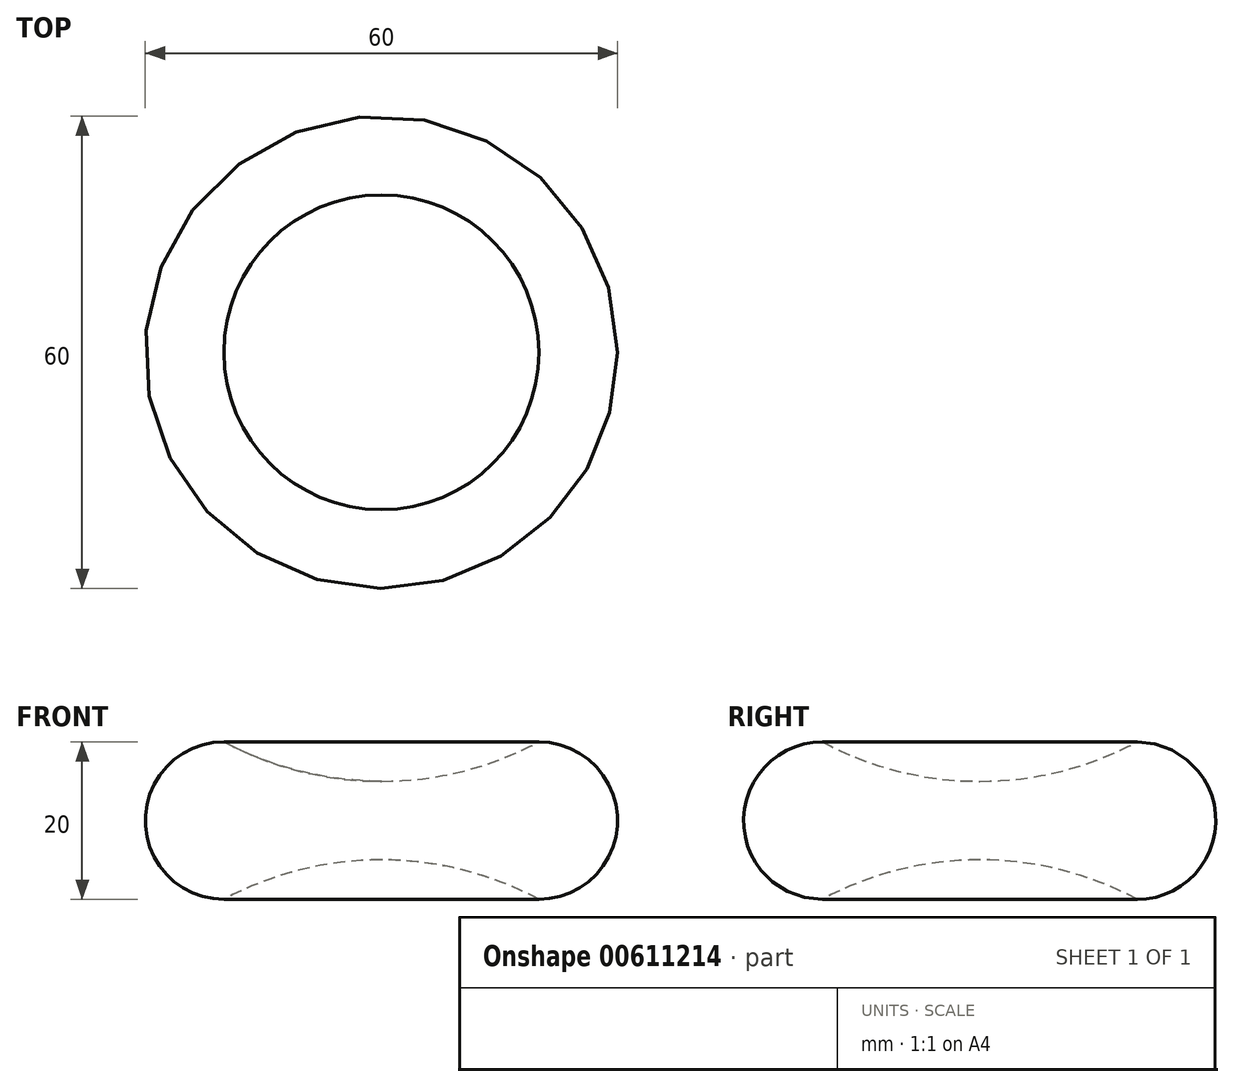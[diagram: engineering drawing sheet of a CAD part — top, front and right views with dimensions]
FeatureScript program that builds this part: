
annotation { "Feature Type Name" : "Feature", "Feature Type Description" : "" }
export const myFeature = defineFeature(function(context is Context, id is Id, definition is map)
    precondition{}
    {
        {
            var Q0;
            Q0=qCreatedBy(makeId("Front.planeOp"),FACE);
            var sketch = newSketch(context, id + "F0", { "sketchPlane" : qUnion([Q0])});
            skArc(sketch, "E0", {"start": v(6.73, -1.4) * mm, "mid": v(16.73, 8.6) * mm, "end": v(6.73, 18.6) * mm});
            skLineSegment(sketch, "E1", {"start": v(-13.27, 13.6) * mm, "end": v(-13.27, 3.6) * mm});
            skArc(sketch, "E2", {"start": v(-13.27, 3.6) * mm, "mid": v(-2.97, 2.33) * mm, "end": v(6.73, -1.4) * mm});
            skArc(sketch, "E3", {"start": v(-13.27, 13.6) * mm, "mid": v(-2.97, 14.87) * mm, "end": v(6.73, 18.6) * mm});
            skSolve(sketch);
        }
        {
            var Q0;
            Q0 = qSketchRegion(id + "F0", true);
            var Q1;
            Q1=sQuery(id+"F0.wireOp",EDGE,"E1");
            revolve(context, id + "F1", {"entities" : qUnion([Q0]), "axis" : qUnion([Q1]), "revolveType" : RevolveType.FULL});
        }
    });
